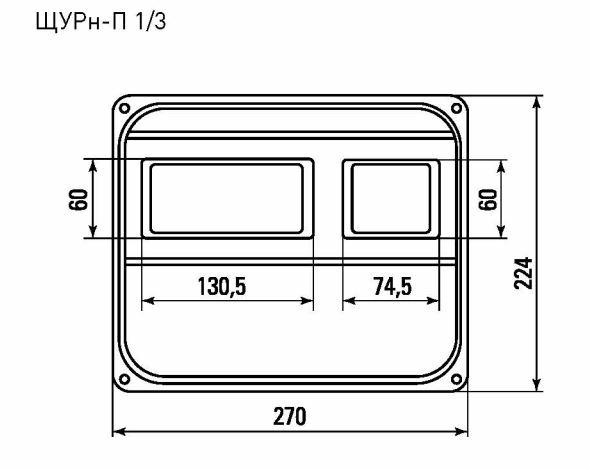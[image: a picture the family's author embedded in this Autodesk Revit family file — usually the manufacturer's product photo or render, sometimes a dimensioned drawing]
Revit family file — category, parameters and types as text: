
# Revit family: EKF_EE_ЩУРн_IP31_Basic
name_source: partatom
category: Электрооборудование
units: mm (PartAtom-declared; Revit-internal decimal feet)

## family parameters
Всегда вертикально = Да
На основе рабочей плоскости = Нет
Общий = Нет
При загрузке вырезать с полостями = Нет
Размер круглого соединителя = Использовать диаметр
Тип детали = Силовой щит
Точка расчета площади = Да

## types (5) — shared parameters
ADSK_Единица измерения = компл.
ADSK_Завод-изготовитель = EKF
ADSK_Классификация нагрузок = Прочее
ADSK_Количество = 1
ADSK_Количество фаз = 3
ADSK_Коэффициент мощности = 1
ADSK_Материал = RAL 7035_Сталь
ADSK_Напряжение = 400 В
ADSK_Номинальная мощность = 0 Вт
ADSK_Полная мощность = 0 В·А
ADSK_Ток = 125 А
Изготовитель = EKF
Количество DIN-реек = 1
Серия номенклатуры = Basic
Степень защиты IP = IP31
ТВ = EKF
Тип установки = Навесной
zero-valued in all types: Количество модулей на DIN-рейке, Максимальное количество модулей

## per-type parameters (varying)
| type | ADSK_Код изделия | ADSK_Марка | ADSK_Масса | ADSK_Наименование | ADSK_Обозначение | ADSK_Размер_Высота | ADSK_Размер_Глубина | ADSK_Размер_Ширина | Описание | Тип |
| ЩУРн 1/9 (400х300х140) IP31 EKF Basic | mb23-1/9-bas | ЩУРн 1/9 IP31 | 4.38 | Щит учетно-распред. навесной ЩУРн 1/9 (400х300х140) IP31 EKF Basic | ЩУРн 1/9 IP31 | 400 мм | 140 мм | 300 мм | Щит учетно-распред. навесной ЩУРн 1/9 (400х300х140) IP31 EKF Basic | 16 мм |
| ЩУРн 1/12 (400x300x140) IP31 EKF Basic | mb23-1/12-bas | ЩУРн 1/12 IP31 | 4.38 | Щит учетно-распред. навесной ЩУРн 1/12 (400x300x140) IP31 EKF Basic | ЩУРн 1/12 IP31 | 400 мм | 140 мм | 300 мм | Щит учетно-распред. навесной ЩУРн 1/12 (400x300x140) IP31 EKF Basic | 18 мм |
| ЩУРн 3/12 (500х300х160) IP31 EKF Basic | mb23-3/12-bas | ЩУРн 3/12 IP31 | 5.88 | Щит учетно-распред. навесной ЩУРн 3/12 (500х300х160) IP31 EKF Basic | ЩУРн 3/12 IP31 | 500 мм | 160 мм | 300 мм | Щит учетно-распред. навесной ЩУРн 3/12 (500х300х160) IP31 EKF Basic | 22 мм |
| ЩУРн 3/24 (500х400х160) IP31 EKF Basic | mb23-3/24-bas | ЩУРн 3/24 IP31 | 7.5 | Щит учетно-распред. навесной ЩУРн 3/24 (500х400х160) IP31 EKF Basic | ЩУРн 3/24 IP31 | 500 мм | 160 мм | 400 мм | Щит учетно-распред. навесной ЩУРн 3/24 (500х400х160) IP31 EKF Basic | 27 мм |
| ЩУРн 1/12 (Э) (360х280х110) IP31 EKF Basic | mb23-1/12e-bas | ЩУРн 1/12 (Э) IP31 | 3.5 | Щит учетно-распред. навесной счетчик на дин-рейку ЩУРн 1/12 (Э) (360х280х110) IP31 EKF Basic | ЩУРн 1/12 (Э) IP31 | 360 мм | 110 мм | 280 мм | Щит учетно-распред. навесной счетчик на дин-рейку ЩУРн 1/12 (Э) (360х280х110) IP31 EKF Basic | 39 мм |
